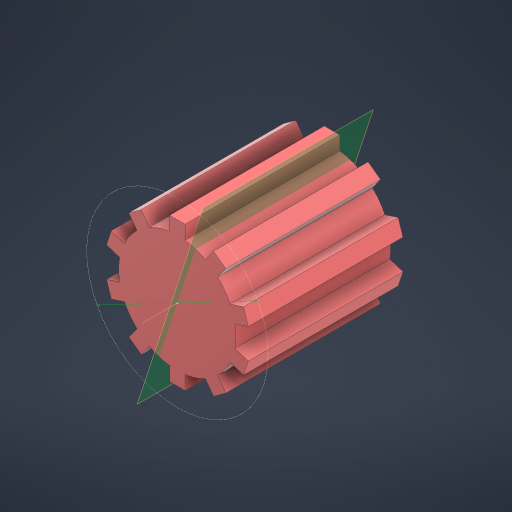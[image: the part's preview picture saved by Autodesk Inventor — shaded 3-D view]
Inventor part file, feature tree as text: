
AUTODESK INVENTOR PART (.ipt)
format: ipt  version: 2024 (Build 280153000, 153)  size: 328,192 bytes
history: native  units: in
note: dims shown in document units (in); Inventor stores cm internally (conversion verified against a paired STEP export)
features: sketch x5, extrude x3, plane x2, projected_geometry x1
ambient origin geometry x8: Origin, YZ Plane, XZ Plane, XY Plane, X Axis, Y Axis, Z Axis, Center Point
bodies: Solid1 (feature_tree)
feature tree (11):
  extrude  "Extrusion1"  Depth=3.937in TaperAngle=360.0deg
  extrude  "Extrusion2"  Depth=0.4331in TaperAngle=0.0deg
  extrude  "Extrusion3"  Depth=0.3543in TaperAngle=0.0deg
  plane  "Work Plane1"
  sketch  "Sketch4"  dims[d14=0.1969in]
  plane  "Work Plane2"
  sketch  "Sketch5"  dims[d15=0.4331in d16=1.3386in d17=0.6693in d18=0.0in d19=1.3386in d24=0.1021in d25=0.1138in]
  sketch  "Sketch1"  dims[d1=1.1811in d3=3.937in d5=360.0deg]
  sketch  "Sketch2"  dims[d7=1.1417in d8=0.0in d9=0.4331in d10=0.0in]
  projected_geometry  "Projected Loop1"
  sketch  "Sketch3"  dims[d11=0.1969in d12=0.3543in d13=0.0in]
